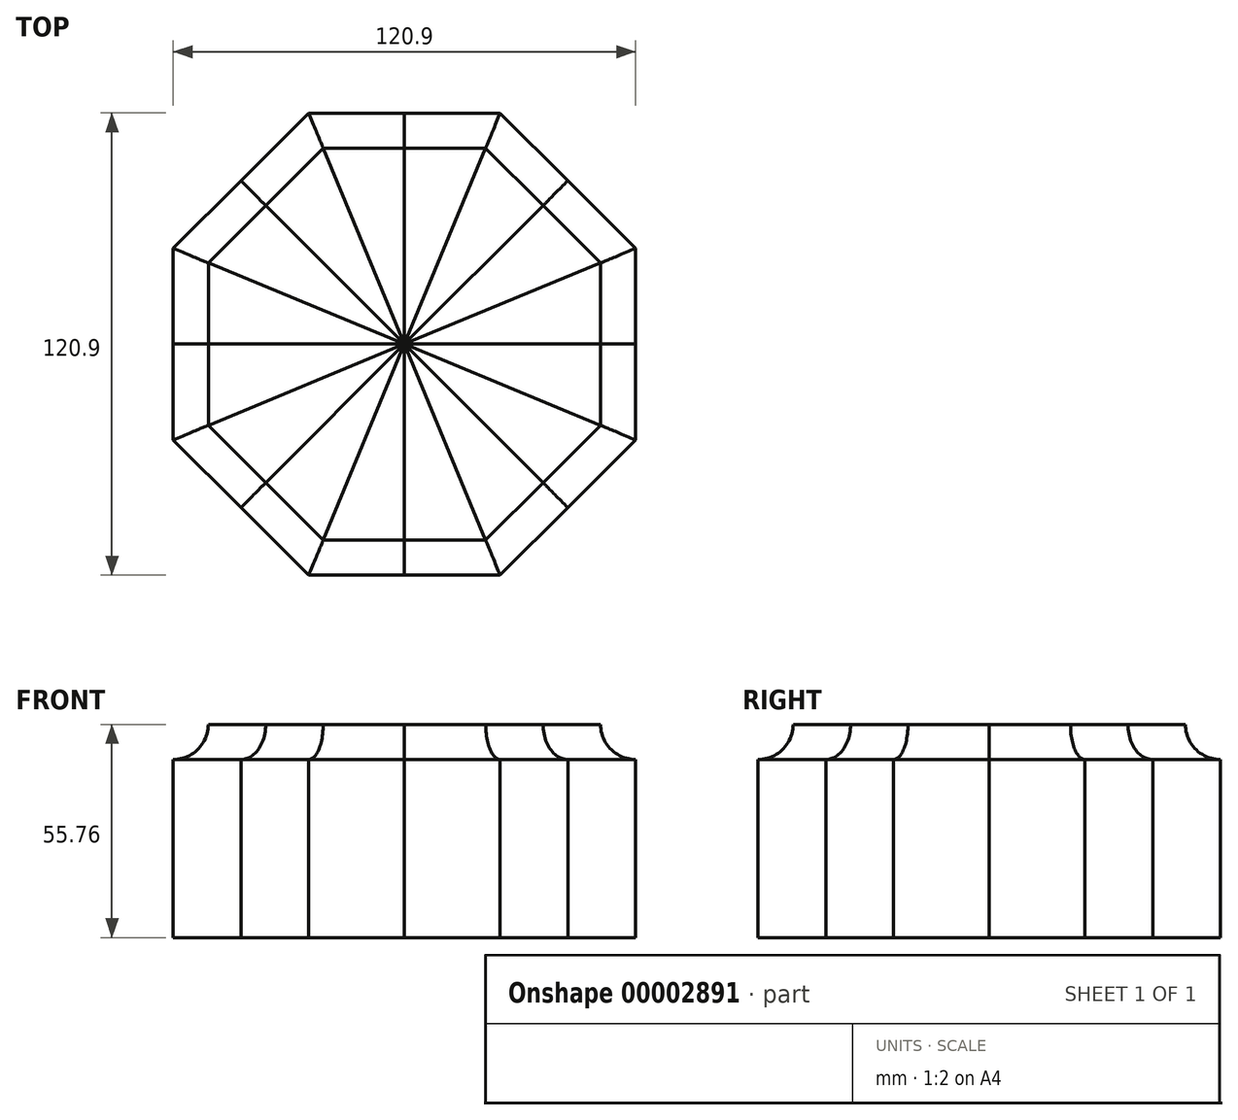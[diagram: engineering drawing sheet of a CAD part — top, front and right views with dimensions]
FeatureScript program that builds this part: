
annotation { "Feature Type Name" : "Feature", "Feature Type Description" : "" }
export const myFeature = defineFeature(function(context is Context, id is Id, definition is map)
    precondition{}
    {
        {
            var Q0;
            Q0=qCreatedBy(makeId("Front.planeOp"),FACE);
            var sketch = newSketch(context, id + "F0", { "sketchPlane" : qUnion([Q0])});
            skLineSegment(sketch, "E0", {"start": v(0, 69.37) * mm, "end": v(0, -35.08) * mm});
            skSolve(sketch);
        }
        {
            var Q0;
            Q0=sQuery(id+"F0.wireOp",EDGE,"E0");
            cPlane(context, id + "F1", {"entities" : qUnion([Q0]), "cplaneType" : CPlaneType.LINE_ANGLE, "offset" : 150 * mm, "angle" : 67.5 * degree, "width" : 150 * mm, "height" : 150 * mm});
        }
        {
            var Q0;
            Q0=qCreatedBy(makeId("Front.planeOp"),FACE);
            var sketch = newSketch(context, id + "F2", { "sketchPlane" : qUnion([Q0])});
            skLineSegment(sketch, "E1.bottom", {"start": v(0, 55.76) * mm, "end": v(-60.45, 55.76) * mm});
            skLineSegment(sketch, "E1.top", {"start": v(0, 0) * mm, "end": v(-60.45, 0) * mm});
            skLineSegment(sketch, "E1.left", {"start": v(0, 55.76) * mm, "end": v(0, 0) * mm});
            skLineSegment(sketch, "E1.right", {"start": v(-60.45, 55.76) * mm, "end": v(-60.45, 0) * mm});
            skCircle(sketch, "E2", {"center": v(-60.45, 55.76) * mm, "radius": 9.19 * mm});
            skSolve(sketch);
        }
        {
            var Q0;
            {var subQ5=sQuery(id+"F2.wireOp",EDGE,"E1.top");Q0=makeQuery(id+"F2.imprint","IMPRINT",FACE,{"disambiguationData":[TD([[makeQuery(id+"F2.imprint","IMPRINT",EDGE,{"derivedFrom":subQ5}),-1.0]])]});}
            var Q1;
            Q1=qCreatedBy(id+"F1.planeOp",FACE);
            extrude(context, id + "F3", {"entities" : qUnion([Q0]), "endBound" : BoundingType.UP_TO_SURFACE, "endBoundEntityFace" : qUnion([Q1]), "depth" : 25 * mm});
        }
        {
            var Q0;
            Q0=makeQuery(id+"F3.opExtrude","SWEPT_BODY",BODY,{"disambiguationData":[OSD([sQuery(id+"F2.wireOp",EDGE,"E1.bottom"),sQuery(id+"F2.wireOp",EDGE,"E1.top"),sQuery(id+"F2.wireOp",EDGE,"E1.left"),sQuery(id+"F2.wireOp",EDGE,"E1.right"),sQuery(id+"F2.wireOp",EDGE,"E2")])]});
            var Q1;
            Q1=qCreatedBy(makeId("Front.planeOp"),FACE);
            mirror(context, id + "F4", {"entities" : qUnion([Q0]), "mirrorPlane" : qUnion([Q1])});
        }
        {
            var Q0;
            Q0=makeQuery(id+"F4.opPattern","COPY",BODY,{"derivedFrom":makeQuery(id+"F3.opExtrude","SWEPT_BODY",BODY,{"disambiguationData":[OSD([sQuery(id+"F2.wireOp",EDGE,"E1.bottom"),sQuery(id+"F2.wireOp",EDGE,"E1.top"),sQuery(id+"F2.wireOp",EDGE,"E1.left"),sQuery(id+"F2.wireOp",EDGE,"E1.right"),sQuery(id+"F2.wireOp",EDGE,"E2")])]}),"instanceName":"1"});
            var Q1;
            Q1=makeQuery(id+"F3.opExtrude","SWEPT_BODY",BODY,{"disambiguationData":[OSD([sQuery(id+"F2.wireOp",EDGE,"E1.bottom"),sQuery(id+"F2.wireOp",EDGE,"E1.top"),sQuery(id+"F2.wireOp",EDGE,"E1.left"),sQuery(id+"F2.wireOp",EDGE,"E1.right"),sQuery(id+"F2.wireOp",EDGE,"E2")])]});
            var Q2;
            Q2=sQuery(id+"F0.wireOp",EDGE,"E0");
            circularPattern(context, id + "F5", {"entities" : qUnion([Q0, Q1]), "axis" : qUnion([Q2]), "angle" : 360 * degree, "instanceCount" : 8, "equalSpace" : true});
        }
    });
